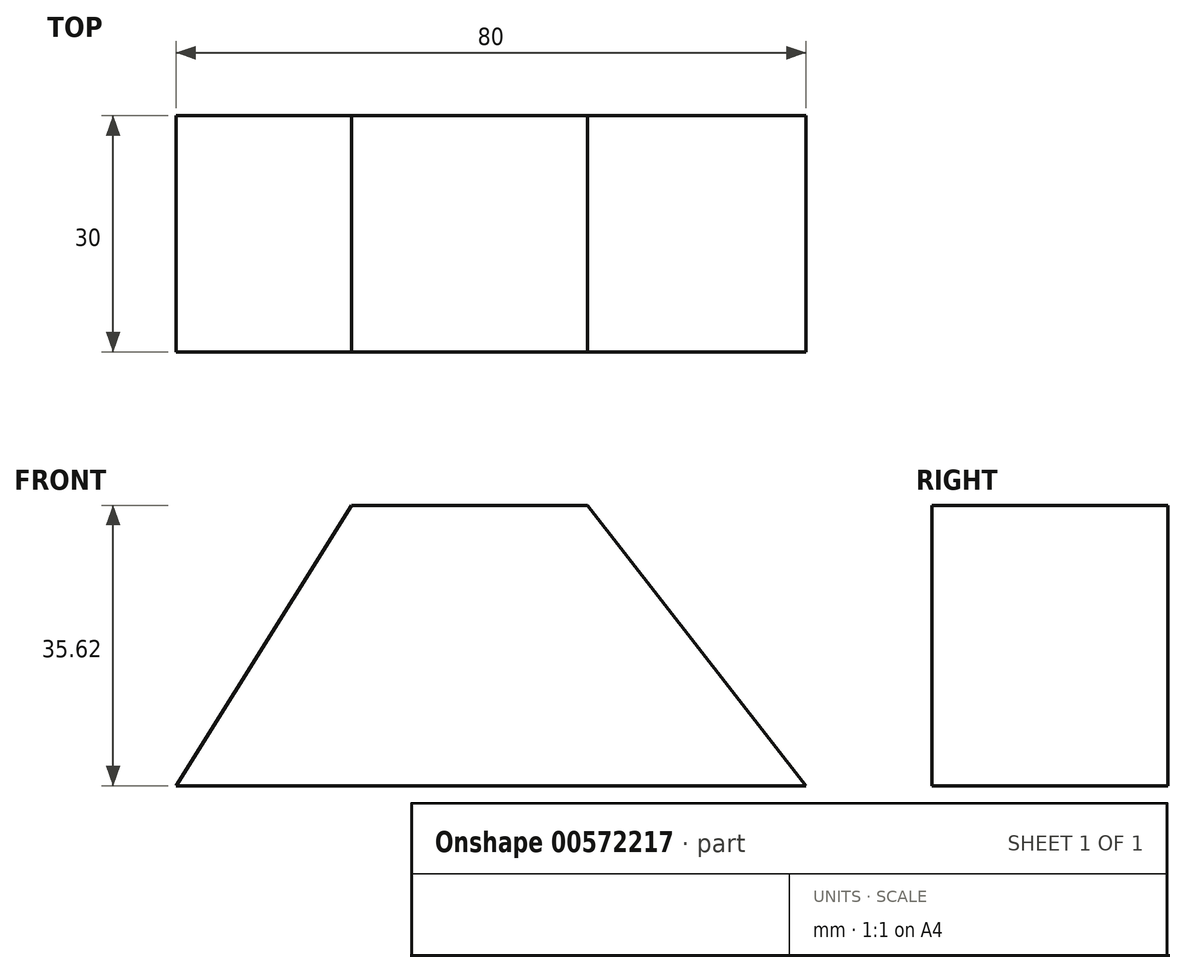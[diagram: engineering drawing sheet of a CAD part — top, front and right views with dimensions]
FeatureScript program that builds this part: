
annotation { "Feature Type Name" : "Feature", "Feature Type Description" : "" }
export const myFeature = defineFeature(function(context is Context, id is Id, definition is map)
    precondition{}
    {
        {
            var Q0;
            Q0=qCreatedBy(makeId("Front.planeOp"),FACE);
            var sketch = newSketch(context, id + "F0", { "sketchPlane" : qUnion([Q0])});
            skLineSegment(sketch, "E0", {"start": v(-67.2, -51.74) * mm, "end": v(12.8, -51.74) * mm});
            skLineSegment(sketch, "E1", {"start": v(12.8, -51.74) * mm, "end": v(-14.94, -16.12) * mm});
            skLineSegment(sketch, "E2", {"start": v(-14.94, -16.12) * mm, "end": v(-44.94, -16.12) * mm});
            skLineSegment(sketch, "E3", {"start": v(-44.94, -16.12) * mm, "end": v(-67.2, -51.74) * mm});
            skSolve(sketch);
        }
        {
            var Q0;
            Q0 = qSketchRegion(id + "F0", true);
            extrude(context, id + "F1", {"entities" : qUnion([Q0]), "depth" : 30 * mm, "offsetDistance" : 25 * mm});
        }
    });
